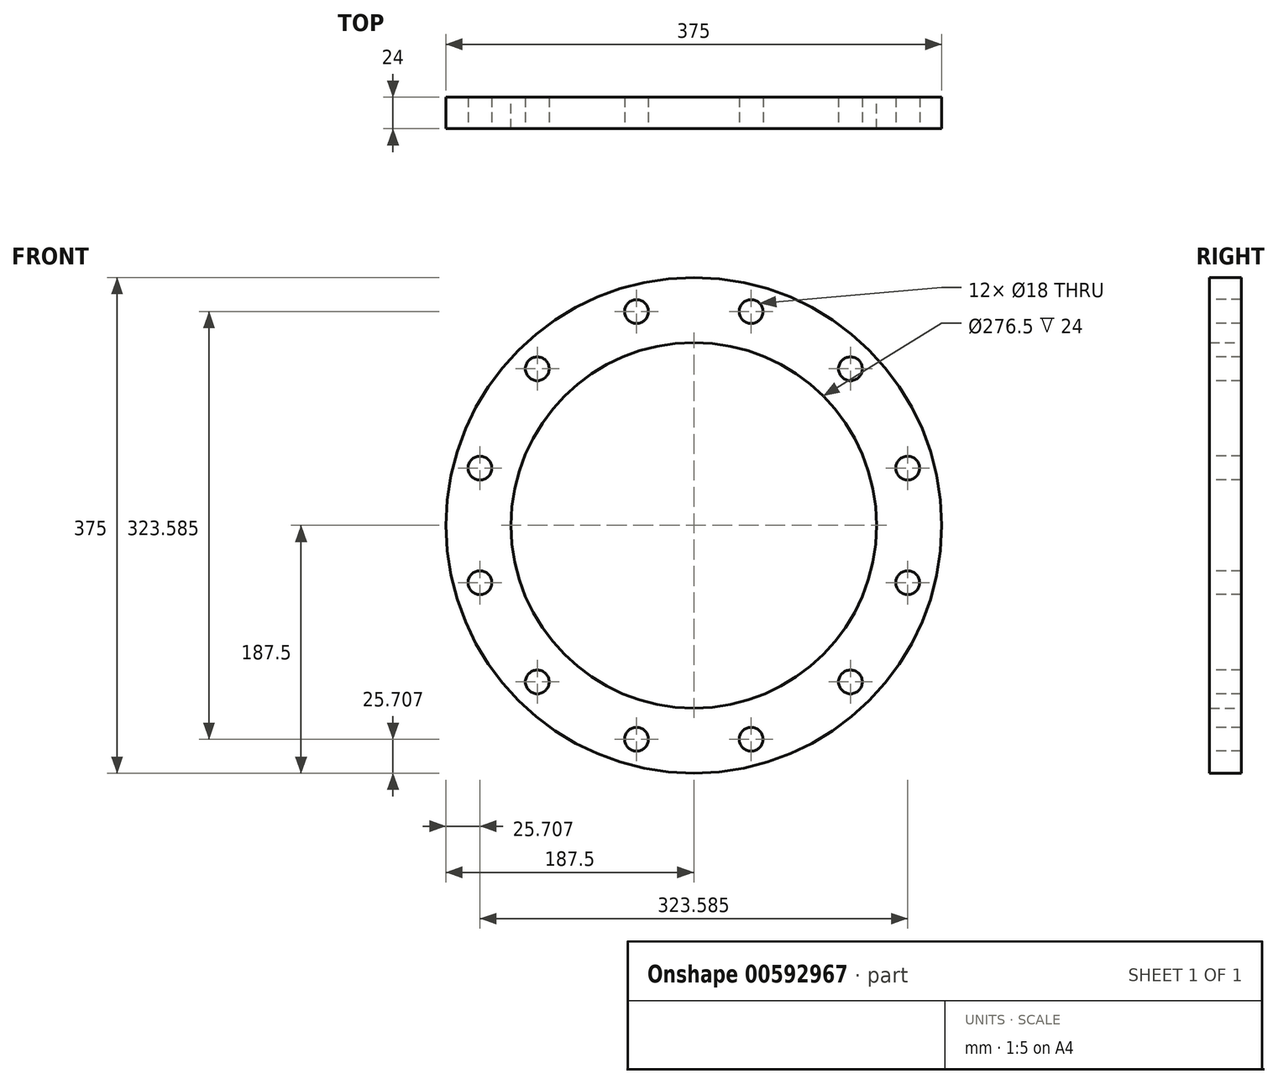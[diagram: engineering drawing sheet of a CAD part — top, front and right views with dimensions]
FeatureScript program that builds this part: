
annotation { "Feature Type Name" : "Feature", "Feature Type Description" : "" }
export const myFeature = defineFeature(function(context is Context, id is Id, definition is map)
    precondition{}
    {
        {
            var Q0;
            Q0=qCreatedBy(makeId("Front.planeOp"),FACE);
            var sketch = newSketch(context, id + "F0", { "sketchPlane" : qUnion([Q0])});
            skCircle(sketch, "E0", {"center": v(0, 0) * mm, "radius": 138.25 * mm});
            skCircle(sketch, "E1", {"center": v(0, 0) * mm, "radius": 187.5 * mm});
            skSolve(sketch);
        }
        {
            var Q0;
            Q0=makeQuery(id+"F0.imprint","IMPRINT",FACE,{"disambiguationData":[TD([[makeQuery(id+"F0.imprint","IMPRINT",EDGE,{"derivedFrom":sQuery(id+"F0.wireOp",EDGE,"E0")}),-1.0]])]});
            extrude(context, id + "F1", {"entities" : qUnion([Q0]), "endBound" : BoundingType.SYMMETRIC, "depth" : 24 * mm, "offsetDistance" : 25 * mm});
        }
        {
            var Q0;
            Q0=qCreatedBy(makeId("Front.planeOp"),FACE);
            var sketch = newSketch(context, id + "F2", { "sketchPlane" : qUnion([Q0])});
            skCircle(sketch, "E2", {"center": v(43.35, 161.8) * mm, "radius": 9 * mm});
            skCircle(sketch, "E3", {"center": v(0, 0) * mm, "radius": 167.5 * mm, "construction": true});
            skCircle(sketch, "E4.1.0", {"center": v(-43.35, 161.8) * mm, "radius": 9 * mm});
            skCircle(sketch, "E4.2.0", {"center": v(-118.44, 118.44) * mm, "radius": 9 * mm});
            skCircle(sketch, "E5.1.3.0", {"center": v(-161.8, 43.35) * mm, "radius": 9 * mm});
            skCircle(sketch, "E5.1.4.0", {"center": v(-161.8, -43.35) * mm, "radius": 9 * mm});
            skCircle(sketch, "E5.1.5.0", {"center": v(-118.44, -118.44) * mm, "radius": 9 * mm});
            skCircle(sketch, "E5.1.6.0", {"center": v(-43.35, -161.8) * mm, "radius": 9 * mm});
            skCircle(sketch, "E5.1.7.0", {"center": v(43.35, -161.8) * mm, "radius": 9 * mm});
            skCircle(sketch, "E5.1.8.0", {"center": v(118.44, -118.44) * mm, "radius": 9 * mm});
            skCircle(sketch, "E5.1.9.0", {"center": v(161.8, -43.35) * mm, "radius": 9 * mm});
            skCircle(sketch, "E5.1.10.0", {"center": v(161.8, 43.35) * mm, "radius": 9 * mm});
            skCircle(sketch, "E5.1.11.0", {"center": v(118.44, 118.44) * mm, "radius": 9 * mm});
            skLineSegment(sketch, "E6", {"start": v(0, 0) * mm, "end": v(0, 167.5) * mm, "construction": true});
            skSolve(sketch);
        }
        {
            var Q0;
            Q0 = qSketchRegion(id + "F2", true);
            extrude(context, id + "F3", {"entities" : qUnion([Q0]), "operationType" : NewBodyOperationType.REMOVE, "endBound" : BoundingType.UP_TO_NEXT, "oppositeDirection" : true, "depth" : 5 * mm, "offsetDistance" : 25 * mm, "hasSecondDirection" : true, "secondDirectionBound" : SecondDirectionBoundingType.UP_TO_NEXT, "secondDirectionOppositeDirection" : false, "secondDirectionDepth" : 25 * mm});
        }
    });
